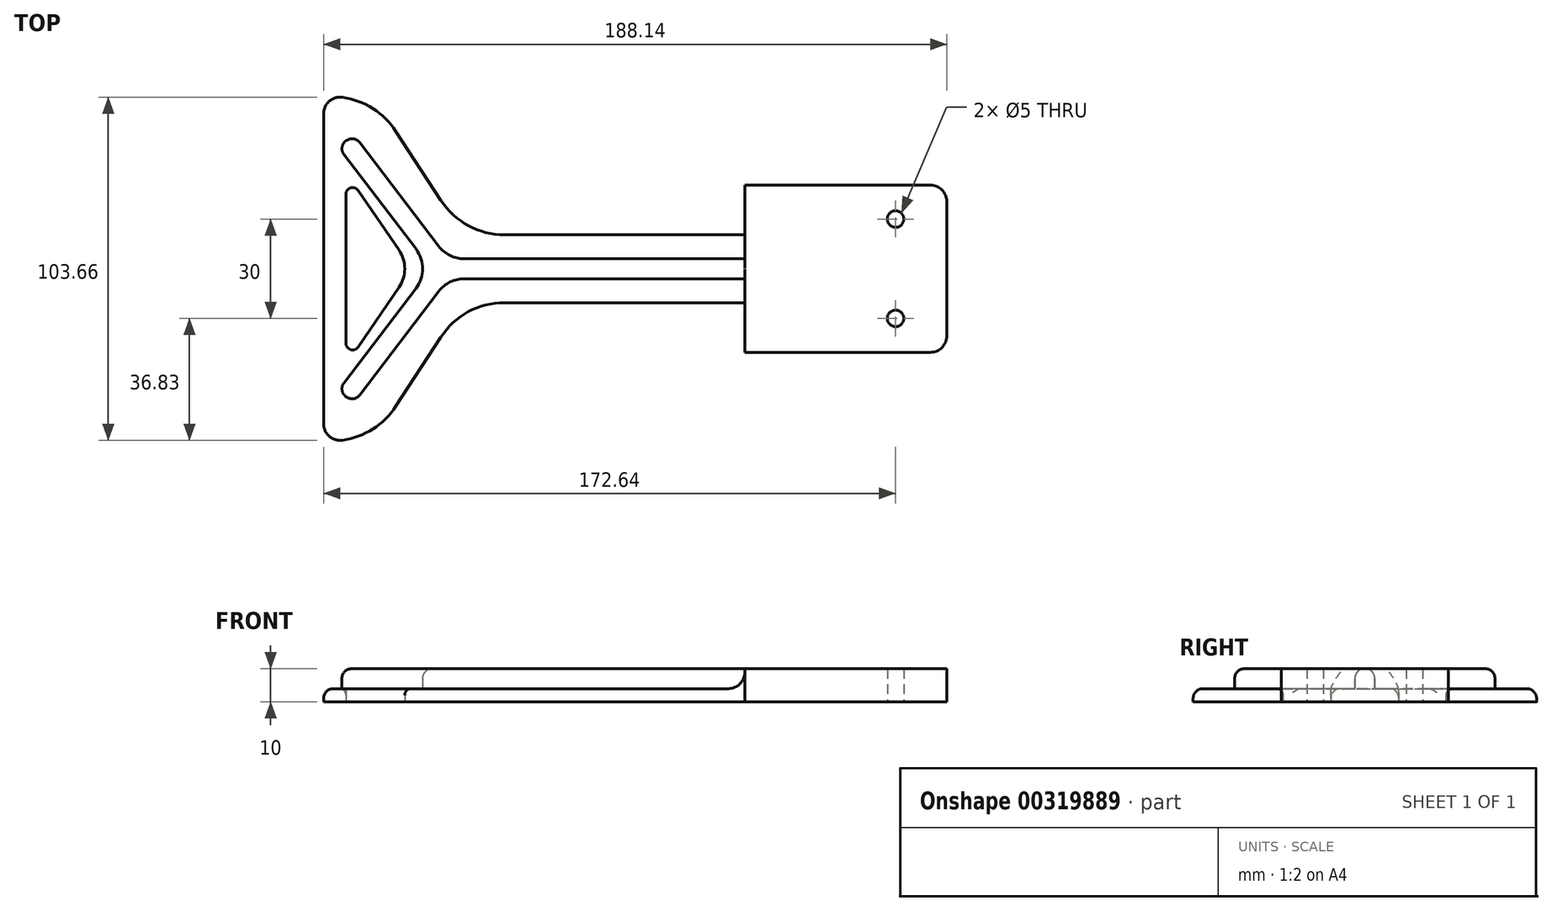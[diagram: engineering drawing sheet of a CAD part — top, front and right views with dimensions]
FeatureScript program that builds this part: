
annotation { "Feature Type Name" : "Feature", "Feature Type Description" : "" }
export const myFeature = defineFeature(function(context is Context, id is Id, definition is map)
    precondition{}
    {
        {
            var Q0;
            Q0=qCreatedBy(makeId("Top.planeOp"),FACE);
            var sketch = newSketch(context, id + "F0", { "sketchPlane" : qUnion([Q0])});
            skLineSegment(sketch, "E0.bottom", {"start": v(25.5, 25.25) * mm, "end": v(-30.5, 25.25) * mm});
            skLineSegment(sketch, "E0.top", {"start": v(25.5, -25.25) * mm, "end": v(-30.5, -25.25) * mm});
            skLineSegment(sketch, "E0.left", {"start": v(30.5, 20.25) * mm, "end": v(30.5, -20.25) * mm});
            skLineSegment(sketch, "E0.right", {"start": v(-30.5, 25.25) * mm, "end": v(-30.5, -25.25) * mm});
            skPoint(sketch, "E0.middle", {"position": v(0, 0) * mm});
            skCircle(sketch, "E1", {"center": v(15, 15) * mm, "radius": 2.5 * mm});
            skCircle(sketch, "E2", {"center": v(15, -15) * mm, "radius": 2.5 * mm});
            skPoint(sketch, "E3.visualSharp", {"position": v(30.5, 25.25) * mm});
            skArc(sketch, "E3.filletArc", {"start": v(30.5, 20.25) * mm, "mid": v(29.04, 23.79) * mm, "end": v(25.5, 25.25) * mm});
            skPoint(sketch, "E4.visualSharp", {"position": v(30.5, -25.25) * mm});
            skArc(sketch, "E4.filletArc", {"start": v(25.5, -25.25) * mm, "mid": v(29.04, -23.79) * mm, "end": v(30.5, -20.25) * mm});
            skPoint(sketch, "E5.positionSnap0", {"position": v(-30.5, 0) * mm});
            skLineSegment(sketch, "E6", {"start": v(-30.5, -10.25) * mm, "end": v(-103.02, -10.25) * mm});
            skLineSegment(sketch, "E7", {"start": v(-122.3, -20.71) * mm, "end": v(-135.84, -41.54) * mm});
            skLineSegment(sketch, "E8", {"start": v(-155.12, -52) * mm, "end": v(-157.64, -52) * mm});
            skLineSegment(sketch, "E9", {"start": v(-157.64, -52) * mm, "end": v(-157.64, 52) * mm});
            skLineSegment(sketch, "E10", {"start": v(-157.64, 52) * mm, "end": v(-155.12, 52) * mm});
            skLineSegment(sketch, "E11", {"start": v(-135.84, 41.54) * mm, "end": v(-122.3, 20.71) * mm});
            skLineSegment(sketch, "E12", {"start": v(-103.02, 10.25) * mm, "end": v(-30.5, 10.25) * mm});
            skPoint(sketch, "E13.visualSharp", {"position": v(-142.64, 52) * mm});
            skArc(sketch, "E13.filletArc", {"start": v(-135.84, 41.54) * mm, "mid": v(-144.15, 49.22) * mm, "end": v(-155.12, 52) * mm});
            skPoint(sketch, "E14.visualSharp", {"position": v(-142.64, -52) * mm});
            skArc(sketch, "E14.filletArc", {"start": v(-155.12, -52) * mm, "mid": v(-144.15, -49.22) * mm, "end": v(-135.84, -41.54) * mm});
            skPoint(sketch, "E15.visualSharp", {"position": v(-115.5, -10.25) * mm});
            skArc(sketch, "E15.filletArc", {"start": v(-103.02, -10.25) * mm, "mid": v(-113.99, -13.03) * mm, "end": v(-122.3, -20.71) * mm});
            skPoint(sketch, "E16.visualSharp", {"position": v(-115.5, 10.25) * mm});
            skArc(sketch, "E16.filletArc", {"start": v(-122.3, 20.71) * mm, "mid": v(-113.99, 13.03) * mm, "end": v(-103.02, 10.25) * mm});
            skLineSegment(sketch, "E17", {"start": v(-30.5, 3) * mm, "end": v(-115.15, 3) * mm});
            skLineSegment(sketch, "E18", {"start": v(-122.9, 6.83) * mm, "end": v(-148.5, 40.44) * mm});
            skLineSegment(sketch, "E19", {"start": v(-30.5, -3) * mm, "end": v(-115.15, -3) * mm});
            skLineSegment(sketch, "E20", {"start": v(-122.9, -6.83) * mm, "end": v(-148.5, -40.44) * mm});
            skLineSegment(sketch, "E21", {"start": v(-148.5, -40.44) * mm, "end": v(-153.27, -36.8) * mm});
            skLineSegment(sketch, "E22", {"start": v(-153.27, -36.8) * mm, "end": v(-129.72, -5.9) * mm});
            skLineSegment(sketch, "E23", {"start": v(-129.72, 5.9) * mm, "end": v(-153.27, 36.8) * mm});
            skLineSegment(sketch, "E24", {"start": v(-153.27, 36.8) * mm, "end": v(-148.5, 40.44) * mm});
            skPoint(sketch, "E25.visualSharp", {"position": v(-125.23, 0) * mm});
            skArc(sketch, "E25.filletArc", {"start": v(-129.72, -5.9) * mm, "mid": v(-127.73, 0) * mm, "end": v(-129.72, 5.9) * mm});
            skPoint(sketch, "E26.visualSharp", {"position": v(-119.97, -3) * mm});
            skArc(sketch, "E26.filletArc", {"start": v(-115.15, -3) * mm, "mid": v(-119.47, -4.01) * mm, "end": v(-122.9, -6.83) * mm});
            skPoint(sketch, "E27.visualSharp", {"position": v(-119.97, 3) * mm});
            skArc(sketch, "E27.filletArc", {"start": v(-122.9, 6.83) * mm, "mid": v(-119.47, 4.01) * mm, "end": v(-115.15, 3) * mm});
            skLineSegment(sketch, "E28", {"start": v(-150.89, 29) * mm, "end": v(-150.89, -29) * mm});
            skPoint(sketch, "E28.startSnap0", {"position": v(-150.89, 38.62) * mm});
            skLineSegment(sketch, "E29", {"start": v(-150.89, -29) * mm, "end": v(-134.9, -5.65) * mm});
            skLineSegment(sketch, "E30", {"start": v(-134.9, 5.65) * mm, "end": v(-150.89, 29) * mm});
            skPoint(sketch, "E31.visualSharp", {"position": v(-131.05, 0) * mm});
            skArc(sketch, "E31.filletArc", {"start": v(-134.9, -5.65) * mm, "mid": v(-133.16, 0) * mm, "end": v(-134.9, 5.65) * mm});
            skSolve(sketch);
        }
        {
            var Q0;
            {var subQ1=sQuery(id+"F0.wireOp",EDGE,"E0.bottom");Q0=makeQuery(id+"F0.imprint","IMPRINT",FACE,{"disambiguationData":[TD([[makeQuery(id+"F0.imprint","IMPRINT",EDGE,{"derivedFrom":subQ1}),1.0]])]});}
            extrude(context, id + "F1", {"entities" : qUnion([Q0]), "depth" : 10 * mm});
        }
        {
            var Q0;
            Q0 = qSketchRegion(id + "F0", true);
            extrude(context, id + "F2", {"entities" : qUnion([Q0]), "operationType" : NewBodyOperationType.ADD, "depth" : 4 * mm});
        }
        {
            var Q0;
            {var subQ0=sQuery(id+"F0.wireOp",EDGE,"E0.right");Q0=makeQuery(id+"F2.boolean.opBoolean","INTERSECT",EDGE,{"derivedFrom":[makeQuery(id+"F1.opExtrude","SWEPT_FACE",FACE,{"disambiguationData":[OSD([subQ0])]}),makeQuery(id+"F2.opExtrude","CAP_FACE",FACE,{"disambiguationData":[OSD([sQuery(id+"F0.wireOp",EDGE,"E0.bottom"),sQuery(id+"F0.wireOp",EDGE,"E0.top"),sQuery(id+"F0.wireOp",EDGE,"E0.left"),subQ0,sQuery(id+"F0.wireOp",EDGE,"E1"),sQuery(id+"F0.wireOp",EDGE,"E2"),sQuery(id+"F0.wireOp",EDGE,"E3.filletArc"),sQuery(id+"F0.wireOp",EDGE,"E4.filletArc"),sQuery(id+"F0.wireOp",EDGE,"E6"),sQuery(id+"F0.wireOp",EDGE,"E7"),sQuery(id+"F0.wireOp",EDGE,"E8"),sQuery(id+"F0.wireOp",EDGE,"E9"),sQuery(id+"F0.wireOp",EDGE,"E10"),sQuery(id+"F0.wireOp",EDGE,"E11"),sQuery(id+"F0.wireOp",EDGE,"E12"),sQuery(id+"F0.wireOp",EDGE,"E13.filletArc"),sQuery(id+"F0.wireOp",EDGE,"E14.filletArc"),sQuery(id+"F0.wireOp",EDGE,"E15.filletArc"),sQuery(id+"F0.wireOp",EDGE,"E16.filletArc")])],"isStart":false})]});}
            var Q1;
            Q1=makeQuery(id+"F2.opExtrude","SWEPT_EDGE",EDGE,{"disambiguationData":[OSD([sQuery(id+"F0.wireOp",EDGE,"E9"),sQuery(id+"F0.wireOp",EDGE,"E10")])]});
            var Q2;
            Q2=makeQuery(id+"F2.opExtrude","SWEPT_EDGE",EDGE,{"disambiguationData":[OSD([sQuery(id+"F0.wireOp",EDGE,"E8"),sQuery(id+"F0.wireOp",EDGE,"E9")])]});
            var Q3;
            Q3=makeQuery(id+"F2.opExtrude","SWEPT_EDGE",EDGE,{"disambiguationData":[OSD([sQuery(id+"F0.wireOp",EDGE,"E0.right"),sQuery(id+"F0.wireOp",EDGE,"E6")])]});
            var Q4;
            Q4=makeQuery(id+"F2.opExtrude","SWEPT_EDGE",EDGE,{"disambiguationData":[OSD([sQuery(id+"F0.wireOp",EDGE,"E0.right"),sQuery(id+"F0.wireOp",EDGE,"E12")])]});
            fillet(context, id + "F3", {"entities" : qUnion([Q0, Q1, Q2, Q3, Q4]), "radius" : 5 * mm, "tangentPropagation" : true, "allowEdgeOverflow" : false});
        }
        {
            var Q0;
            {var subQ0=sQuery(id+"F0.wireOp",EDGE,"E17");Q0=makeQuery(id+"F0.imprint","IMPRINT",FACE,{"disambiguationData":[TD([[makeQuery(id+"F0.imprint","IMPRINT",EDGE,{"derivedFrom":subQ0}),1.0]])]});}
            extrude(context, id + "F4", {"entities" : qUnion([Q0]), "operationType" : NewBodyOperationType.ADD, "depth" : 10 * mm});
        }
        {
            var Q0;
            Q0=makeQuery(id+"F4.opExtrude","CAP_EDGE",EDGE,{"disambiguationData":[OSD([sQuery(id+"F0.wireOp",EDGE,"E17")])],"isStart":false});
            var Q1;
            Q1=makeQuery(id+"F4.opExtrude","CAP_EDGE",EDGE,{"disambiguationData":[OSD([sQuery(id+"F0.wireOp",EDGE,"E19")])],"isStart":false});
            var Q2;
            Q2=makeQuery(id+"F4.opExtrude","CAP_EDGE",EDGE,{"disambiguationData":[OSD([sQuery(id+"F0.wireOp",EDGE,"E25.filletArc")])],"isStart":false});
            var Q3;
            Q3=makeQuery(id+"F4.opExtrude","CAP_EDGE",EDGE,{"disambiguationData":[OSD([sQuery(id+"F0.wireOp",EDGE,"E24")])],"isStart":false});
            var Q4;
            Q4=makeQuery(id+"F4.opExtrude","CAP_EDGE",EDGE,{"disambiguationData":[OSD([sQuery(id+"F0.wireOp",EDGE,"E21")])],"isStart":false});
            var Q5;
            Q5=makeQuery(id+"F4.opExtrude","SWEPT_EDGE",EDGE,{"disambiguationData":[OSD([sQuery(id+"F0.wireOp",EDGE,"E20"),sQuery(id+"F0.wireOp",EDGE,"E21")])]});
            var Q6;
            Q6=makeQuery(id+"F4.opExtrude","SWEPT_EDGE",EDGE,{"disambiguationData":[OSD([sQuery(id+"F0.wireOp",EDGE,"E21"),sQuery(id+"F0.wireOp",EDGE,"E22")])]});
            var Q7;
            Q7=makeQuery(id+"F4.opExtrude","SWEPT_EDGE",EDGE,{"disambiguationData":[OSD([sQuery(id+"F0.wireOp",EDGE,"E23"),sQuery(id+"F0.wireOp",EDGE,"E24")])]});
            var Q8;
            Q8=makeQuery(id+"F4.opExtrude","SWEPT_EDGE",EDGE,{"disambiguationData":[OSD([sQuery(id+"F0.wireOp",EDGE,"E18"),sQuery(id+"F0.wireOp",EDGE,"E24")])]});
            var Q9;
            Q9=makeQuery(id+"F2.opExtrude","CAP_EDGE",EDGE,{"disambiguationData":[OSD([sQuery(id+"F0.wireOp",EDGE,"E6")])],"isStart":false});
            fillet(context, id + "F5", {"entities" : qUnion([Q0, Q1, Q2, Q3, Q4, Q5, Q6, Q7, Q8, Q9]), "radius" : 2.9 * mm, "tangentPropagation" : true, "allowEdgeOverflow" : false});
        }
        {
            var Q0;
            Q0=makeQuery(id+"F2.opExtrude","SWEPT_EDGE",EDGE,{"disambiguationData":[OSD([sQuery(id+"F0.wireOp",EDGE,"E28"),sQuery(id+"F0.wireOp",EDGE,"E29")])]});
            var Q1;
            Q1=makeQuery(id+"F2.opExtrude","SWEPT_EDGE",EDGE,{"disambiguationData":[OSD([sQuery(id+"F0.wireOp",EDGE,"E28"),sQuery(id+"F0.wireOp",EDGE,"E30")])]});
            var Q2;
            Q2=makeQuery(id+"F2.opExtrude","CAP_EDGE",EDGE,{"disambiguationData":[OSD([sQuery(id+"F0.wireOp",EDGE,"E31.filletArc")])],"isStart":false});
            fillet(context, id + "F6", {"entities" : qUnion([Q0, Q1, Q2]), "radius" : 2 * mm, "tangentPropagation" : true, "allowEdgeOverflow" : false});
        }
    });
